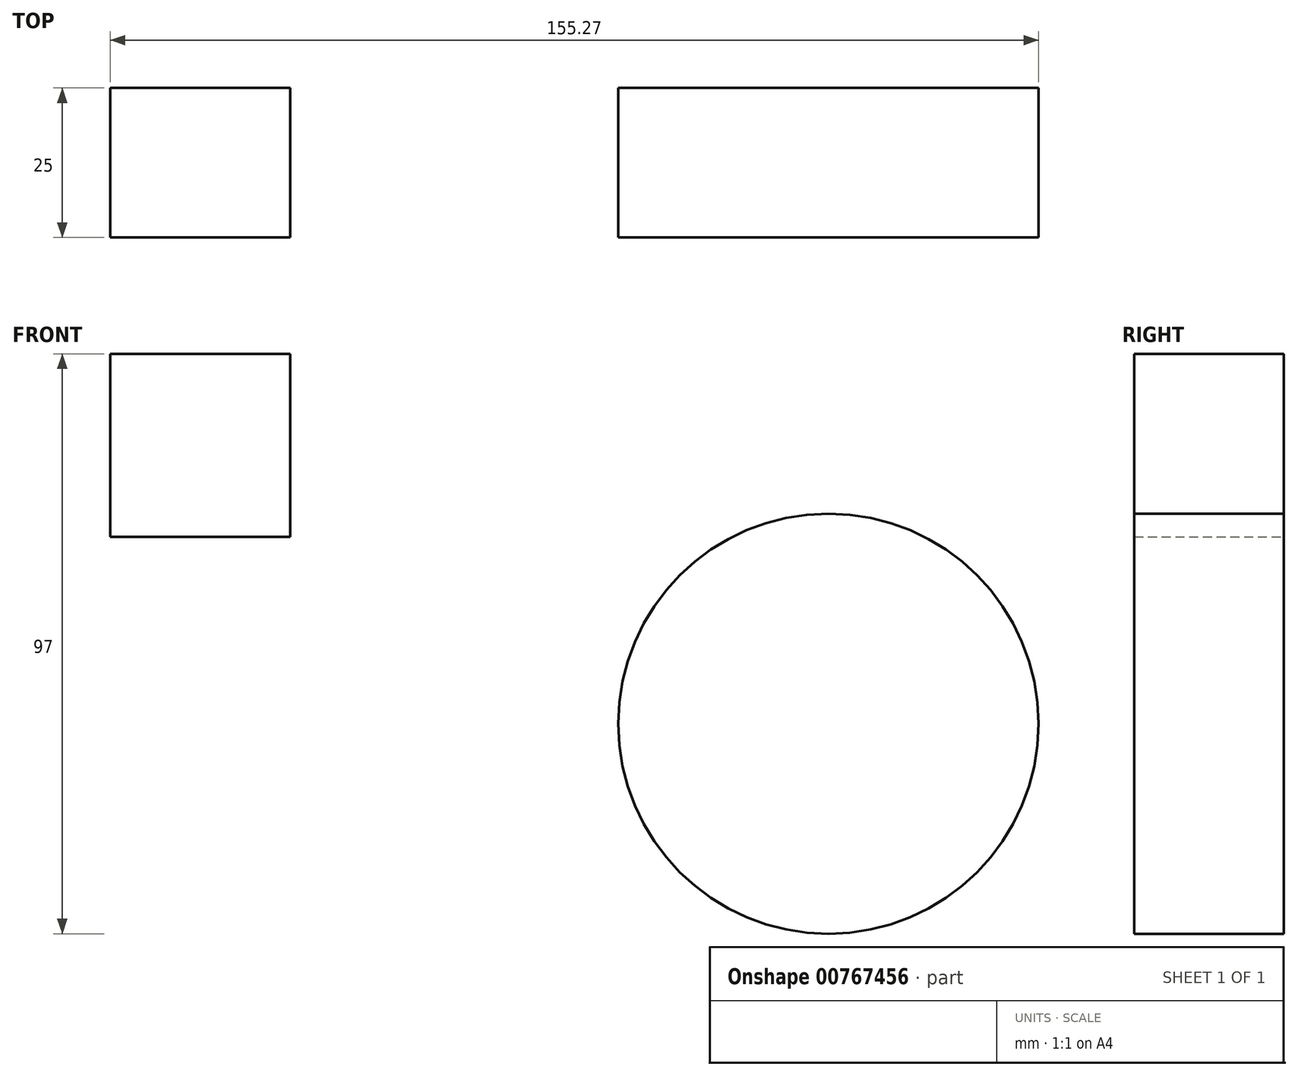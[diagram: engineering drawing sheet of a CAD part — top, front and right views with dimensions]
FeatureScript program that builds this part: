
annotation { "Feature Type Name" : "Feature", "Feature Type Description" : "" }
export const myFeature = defineFeature(function(context is Context, id is Id, definition is map)
    precondition{}
    {
        {
            var Q0;
            Q0=qCreatedBy(makeId("Front.planeOp"),FACE);
            var sketch = newSketch(context, id + "F0", { "sketchPlane" : qUnion([Q0])});
            skCircle(sketch, "E0", {"center": v(0, 0) * mm, "radius": 35.14 * mm});
            skSolve(sketch);
        }
        {
            var Q0;
            Q0 = qSketchRegion(id + "F0", true);
            extrude(context, id + "F1", {"entities" : qUnion([Q0]), "depth" : 25 * mm, "offsetDistance" : 25 * mm});
        }
        {
            var Q0;
            Q0=qCreatedBy(makeId("Front.planeOp"),FACE);
            var sketch = newSketch(context, id + "F2", { "sketchPlane" : qUnion([Q0])});
            skLineSegment(sketch, "E1.bottom", {"start": v(-120.13, 61.86) * mm, "end": v(-90, 61.86) * mm});
            skLineSegment(sketch, "E1.top", {"start": v(-120.13, 31.24) * mm, "end": v(-90, 31.24) * mm});
            skLineSegment(sketch, "E1.left", {"start": v(-120.13, 61.86) * mm, "end": v(-120.13, 31.24) * mm});
            skLineSegment(sketch, "E1.right", {"start": v(-90, 61.86) * mm, "end": v(-90, 31.24) * mm});
            skSolve(sketch);
        }
        {
            var Q0;
            Q0 = qSketchRegion(id + "F2", true);
            extrude(context, id + "F3", {"entities" : qUnion([Q0]), "depth" : 25 * mm, "offsetDistance" : 25 * mm});
        }
    });
